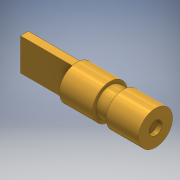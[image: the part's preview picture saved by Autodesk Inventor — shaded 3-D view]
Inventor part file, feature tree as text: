
AUTODESK INVENTOR PART (.ipt)
format: ipt  version: 2016 (Build 200138000, 138)  size: 139,776 bytes
history: native  units: mm
features: sketch x2, revolve x1, extrude x1
ambient origin geometry x8: Origin, YZ Plane, XZ Plane, XY Plane, X Axis, Y Axis, Z Axis, Center Point
bodies: Solid1 (feature_tree)
feature tree (4):
  revolve  "Revolution1"  [1 undecoded]
  extrude  "Extrusion1"  Depth=3.7mm
  sketch  "Sketch1"  dims[d0=4.0mm d1=3.9mm]
  sketch  "Sketch2"  dims[d2=3.8mm d3=3.7mm d4=90.0deg d5=3.2mm d6=3.7mm d7=0.9mm d8=6.0mm d9=0.0mm d10=1.5mm d11=0.5mm]
note: 1 required parameter value undecoded (feature->parameter linkage not recoverable at this tier; creation-order binding heuristic only, values carry confidence <= 0.55)
